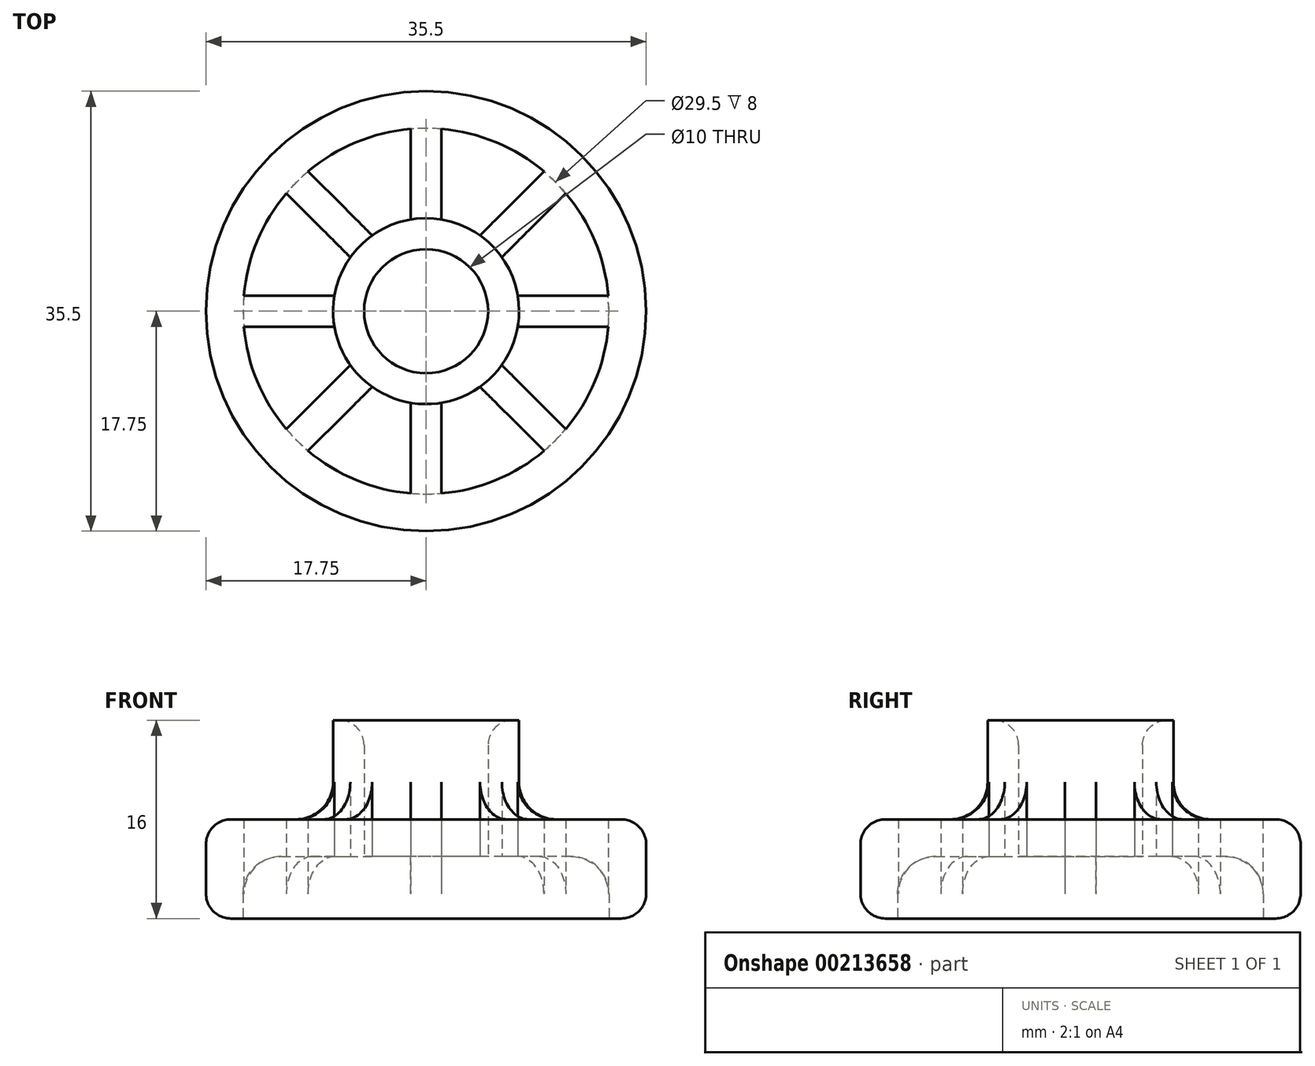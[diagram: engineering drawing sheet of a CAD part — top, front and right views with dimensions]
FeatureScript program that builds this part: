
annotation { "Feature Type Name" : "Feature", "Feature Type Description" : "" }
export const myFeature = defineFeature(function(context is Context, id is Id, definition is map)
    precondition{}
    {
        {
            var Q0;
            Q0=qCreatedBy(makeId("Top.planeOp"),FACE);
            var sketch = newSketch(context, id + "F0", { "sketchPlane" : qUnion([Q0])});
            skCircle(sketch, "E0", {"center": v(0, 0) * mm, "radius": 17.75 * mm});
            skCircle(sketch, "E1", {"center": v(0, 0) * mm, "radius": 14.75 * mm});
            skSolve(sketch);
        }
        {
            var Q0;
            Q0=makeQuery(id+"F0.imprint","IMPRINT",FACE,{"disambiguationData":[TD([[makeQuery(id+"F0.imprint","IMPRINT",EDGE,{"derivedFrom":sQuery(id+"F0.wireOp",EDGE,"E0")}),1.0]])]});
            extrude(context, id + "F1", {"entities" : qUnion([Q0]), "depth" : 8 * mm});
        }
        {
            var Q0;
            Q0=qCreatedBy(makeId("Top.planeOp"),FACE);
            cPlane(context, id + "F2", {"entities" : qUnion([Q0]), "cplaneType" : CPlaneType.OFFSET, "offset" : 5 * mm, "width" : 150 * mm, "height" : 150 * mm});
        }
        {
            var Q0;
            Q0=qCreatedBy(id+"F2.planeOp",FACE);
            var sketch = newSketch(context, id + "F3", { "sketchPlane" : qUnion([Q0])});
            skCircle(sketch, "E2", {"center": v(0, 0) * mm, "radius": 7.5 * mm});
            skCircle(sketch, "E3", {"center": v(0, 0) * mm, "radius": 5 * mm});
            skSolve(sketch);
        }
        {
            var Q0;
            Q0=makeQuery(id+"F3.imprint","IMPRINT",FACE,{"disambiguationData":[TD([[makeQuery(id+"F3.imprint","IMPRINT",EDGE,{"derivedFrom":sQuery(id+"F3.wireOp",EDGE,"E2")}),1.0]])]});
            extrude(context, id + "F4", {"entities" : qUnion([Q0]), "depth" : 11 * mm});
        }
        {
            var Q0;
            Q0=qCreatedBy(id+"F2.planeOp",FACE);
            var sketch = newSketch(context, id + "F5", { "sketchPlane" : qUnion([Q0])});
            skLineSegment(sketch, "E4.bottom", {"start": v(1.25, 15.28) * mm, "end": v(-1.25, 15.28) * mm});
            skLineSegment(sketch, "E4.top", {"start": v(1.25, 6.97) * mm, "end": v(-1.25, 6.97) * mm});
            skLineSegment(sketch, "E4.left", {"start": v(1.25, 15.28) * mm, "end": v(1.25, 6.97) * mm});
            skLineSegment(sketch, "E4.right", {"start": v(-1.25, 15.28) * mm, "end": v(-1.25, 6.97) * mm});
            skPoint(sketch, "E4.middle", {"position": v(0, 11.12) * mm});
            skSolve(sketch);
        }
        {
            var Q0;
            Q0=makeQuery(id+"F5.imprint","IMPRINT",FACE,{"disambiguationData":[TD([[makeQuery(id+"F5.imprint","IMPRINT",EDGE,{"derivedFrom":sQuery(id+"F5.wireOp",EDGE,"E4.bottom")}),1.0]])]});
            extrude(context, id + "F6", {"entities" : qUnion([Q0]), "depth" : 3 * mm});
        }
        {
            var Q0;
            Q0=qCreatedBy(makeId("Front.planeOp"),FACE);
            var sketch = newSketch(context, id + "F7", { "sketchPlane" : qUnion([Q0])});
            skLineSegment(sketch, "E5", {"start": v(0, 47.66) * mm, "end": v(0, -31.66) * mm, "construction": true});
            skSolve(sketch);
        }
        {
            var Q0;
            Q0=makeQuery(id+"F6.opExtrude","SWEPT_BODY",BODY,{"disambiguationData":[OSD([sQuery(id+"F5.wireOp",EDGE,"E4.bottom"),sQuery(id+"F5.wireOp",EDGE,"E4.top"),sQuery(id+"F5.wireOp",EDGE,"E4.left"),sQuery(id+"F5.wireOp",EDGE,"E4.right")])]});
            var Q1;
            Q1=sQuery(id+"F7.wireOp",EDGE,"E5");
            var Q2;
            Q2=makeQuery(id+"F6.opExtrude","SWEPT_BODY",BODY,{"disambiguationData":[OSD([sQuery(id+"F5.wireOp",EDGE,"E4.bottom"),sQuery(id+"F5.wireOp",EDGE,"E4.top"),sQuery(id+"F5.wireOp",EDGE,"E4.left"),sQuery(id+"F5.wireOp",EDGE,"E4.right")])]});
            circularPattern(context, id + "F8", {"operationType" : NewBodyOperationType.ADD, "entities" : qUnion([Q0]), "axis" : qUnion([Q1]), "angle" : 360 * degree, "instanceCount" : 8, "equalSpace" : true});
        }
        {
            var Q0;
            Q0=makeQuery(id+"F8.boolean.opBoolean","INTERSECT",EDGE,{"derivedFrom":[makeQuery(id+"F4.opExtrude","SWEPT_FACE",FACE,{"disambiguationData":[OSD([sQuery(id+"F3.wireOp",EDGE,"E2")])]}),makeQuery(id+"F8.opPattern","COPY",FACE,{"derivedFrom":makeQuery(id+"F6.opExtrude","CAP_FACE",FACE,{"disambiguationData":[OSD([sQuery(id+"F5.wireOp",EDGE,"E4.bottom"),sQuery(id+"F5.wireOp",EDGE,"E4.top"),sQuery(id+"F5.wireOp",EDGE,"E4.left"),sQuery(id+"F5.wireOp",EDGE,"E4.right")])],"isStart":false}),"instanceName":"1"})]});
            var Q1;
            Q1=makeQuery(id+"F8.boolean.opBoolean","INTERSECT",EDGE,{"derivedFrom":[makeQuery(id+"F4.opExtrude","SWEPT_FACE",FACE,{"disambiguationData":[OSD([sQuery(id+"F3.wireOp",EDGE,"E2")])]}),makeQuery(id+"F8.opPattern","COPY",FACE,{"derivedFrom":makeQuery(id+"F6.opExtrude","CAP_FACE",FACE,{"disambiguationData":[OSD([sQuery(id+"F5.wireOp",EDGE,"E4.bottom"),sQuery(id+"F5.wireOp",EDGE,"E4.top"),sQuery(id+"F5.wireOp",EDGE,"E4.left"),sQuery(id+"F5.wireOp",EDGE,"E4.right")])],"isStart":false}),"instanceName":"2"})]});
            var Q2;
            Q2=makeQuery(id+"F8.boolean.opBoolean","INTERSECT",EDGE,{"derivedFrom":[makeQuery(id+"F4.opExtrude","SWEPT_FACE",FACE,{"disambiguationData":[OSD([sQuery(id+"F3.wireOp",EDGE,"E2")])]}),makeQuery(id+"F8.opPattern","COPY",FACE,{"derivedFrom":makeQuery(id+"F6.opExtrude","CAP_FACE",FACE,{"disambiguationData":[OSD([sQuery(id+"F5.wireOp",EDGE,"E4.bottom"),sQuery(id+"F5.wireOp",EDGE,"E4.top"),sQuery(id+"F5.wireOp",EDGE,"E4.left"),sQuery(id+"F5.wireOp",EDGE,"E4.right")])],"isStart":false}),"instanceName":"3"})]});
            var Q3;
            Q3=makeQuery(id+"F8.boolean.opBoolean","INTERSECT",EDGE,{"derivedFrom":[makeQuery(id+"F4.opExtrude","SWEPT_FACE",FACE,{"disambiguationData":[OSD([sQuery(id+"F3.wireOp",EDGE,"E2")])]}),makeQuery(id+"F6.opExtrude","CAP_FACE",FACE,{"disambiguationData":[OSD([sQuery(id+"F5.wireOp",EDGE,"E4.bottom"),sQuery(id+"F5.wireOp",EDGE,"E4.top"),sQuery(id+"F5.wireOp",EDGE,"E4.left"),sQuery(id+"F5.wireOp",EDGE,"E4.right")])],"isStart":false})]});
            var Q4;
            Q4=makeQuery(id+"F8.boolean.opBoolean","INTERSECT",EDGE,{"derivedFrom":[makeQuery(id+"F4.opExtrude","SWEPT_FACE",FACE,{"disambiguationData":[OSD([sQuery(id+"F3.wireOp",EDGE,"E2")])]}),makeQuery(id+"F8.opPattern","COPY",FACE,{"derivedFrom":makeQuery(id+"F6.opExtrude","CAP_FACE",FACE,{"disambiguationData":[OSD([sQuery(id+"F5.wireOp",EDGE,"E4.bottom"),sQuery(id+"F5.wireOp",EDGE,"E4.top"),sQuery(id+"F5.wireOp",EDGE,"E4.left"),sQuery(id+"F5.wireOp",EDGE,"E4.right")])],"isStart":false}),"instanceName":"7"})]});
            var Q5;
            Q5=makeQuery(id+"F8.boolean.opBoolean","INTERSECT",EDGE,{"derivedFrom":[makeQuery(id+"F4.opExtrude","SWEPT_FACE",FACE,{"disambiguationData":[OSD([sQuery(id+"F3.wireOp",EDGE,"E2")])]}),makeQuery(id+"F8.opPattern","COPY",FACE,{"derivedFrom":makeQuery(id+"F6.opExtrude","CAP_FACE",FACE,{"disambiguationData":[OSD([sQuery(id+"F5.wireOp",EDGE,"E4.bottom"),sQuery(id+"F5.wireOp",EDGE,"E4.top"),sQuery(id+"F5.wireOp",EDGE,"E4.left"),sQuery(id+"F5.wireOp",EDGE,"E4.right")])],"isStart":false}),"instanceName":"6"})]});
            var Q6;
            Q6=makeQuery(id+"F8.boolean.opBoolean","INTERSECT",EDGE,{"derivedFrom":[makeQuery(id+"F4.opExtrude","SWEPT_FACE",FACE,{"disambiguationData":[OSD([sQuery(id+"F3.wireOp",EDGE,"E2")])]}),makeQuery(id+"F8.opPattern","COPY",FACE,{"derivedFrom":makeQuery(id+"F6.opExtrude","CAP_FACE",FACE,{"disambiguationData":[OSD([sQuery(id+"F5.wireOp",EDGE,"E4.bottom"),sQuery(id+"F5.wireOp",EDGE,"E4.top"),sQuery(id+"F5.wireOp",EDGE,"E4.left"),sQuery(id+"F5.wireOp",EDGE,"E4.right")])],"isStart":false}),"instanceName":"5"})]});
            var Q7;
            Q7=makeQuery(id+"F8.boolean.opBoolean","INTERSECT",EDGE,{"derivedFrom":[makeQuery(id+"F4.opExtrude","SWEPT_FACE",FACE,{"disambiguationData":[OSD([sQuery(id+"F3.wireOp",EDGE,"E2")])]}),makeQuery(id+"F8.opPattern","COPY",FACE,{"derivedFrom":makeQuery(id+"F6.opExtrude","CAP_FACE",FACE,{"disambiguationData":[OSD([sQuery(id+"F5.wireOp",EDGE,"E4.bottom"),sQuery(id+"F5.wireOp",EDGE,"E4.top"),sQuery(id+"F5.wireOp",EDGE,"E4.left"),sQuery(id+"F5.wireOp",EDGE,"E4.right")])],"isStart":false}),"instanceName":"4"})]});
            var Q8;
            Q8=makeQuery(id+"F8.boolean.opBoolean","INTERSECT",EDGE,{"disambiguationData":[OD(7.0)],"derivedFrom":[makeQuery(id+"F1.opExtrude","SWEPT_FACE",FACE,{"disambiguationData":[OSD([sQuery(id+"F0.wireOp",EDGE,"E1")])]}),makeQuery(id+"F8.opPattern","COPY",FACE,{"derivedFrom":makeQuery(id+"F6.opExtrude","CAP_FACE",FACE,{"disambiguationData":[OSD([sQuery(id+"F5.wireOp",EDGE,"E4.bottom"),sQuery(id+"F5.wireOp",EDGE,"E4.top"),sQuery(id+"F5.wireOp",EDGE,"E4.left"),sQuery(id+"F5.wireOp",EDGE,"E4.right")])],"isStart":true}),"instanceName":"7"})]});
            var Q9;
            Q9=makeQuery(id+"F8.boolean.opBoolean","INTERSECT",EDGE,{"disambiguationData":[OD(0.0)],"derivedFrom":[makeQuery(id+"F1.opExtrude","SWEPT_FACE",FACE,{"disambiguationData":[OSD([sQuery(id+"F0.wireOp",EDGE,"E1")])]}),makeQuery(id+"F8.opPattern","COPY",FACE,{"derivedFrom":makeQuery(id+"F6.opExtrude","CAP_FACE",FACE,{"disambiguationData":[OSD([sQuery(id+"F5.wireOp",EDGE,"E4.bottom"),sQuery(id+"F5.wireOp",EDGE,"E4.top"),sQuery(id+"F5.wireOp",EDGE,"E4.left"),sQuery(id+"F5.wireOp",EDGE,"E4.right")])],"isStart":true}),"instanceName":"7"})]});
            var Q10;
            Q10=makeQuery(id+"F8.boolean.opBoolean","INTERSECT",EDGE,{"disambiguationData":[OD(6.0)],"derivedFrom":[makeQuery(id+"F1.opExtrude","SWEPT_FACE",FACE,{"disambiguationData":[OSD([sQuery(id+"F0.wireOp",EDGE,"E1")])]}),makeQuery(id+"F8.opPattern","COPY",FACE,{"derivedFrom":makeQuery(id+"F6.opExtrude","CAP_FACE",FACE,{"disambiguationData":[OSD([sQuery(id+"F5.wireOp",EDGE,"E4.bottom"),sQuery(id+"F5.wireOp",EDGE,"E4.top"),sQuery(id+"F5.wireOp",EDGE,"E4.left"),sQuery(id+"F5.wireOp",EDGE,"E4.right")])],"isStart":true}),"instanceName":"7"})]});
            var Q11;
            Q11=makeQuery(id+"F8.boolean.opBoolean","INTERSECT",EDGE,{"disambiguationData":[OD(5.0)],"derivedFrom":[makeQuery(id+"F1.opExtrude","SWEPT_FACE",FACE,{"disambiguationData":[OSD([sQuery(id+"F0.wireOp",EDGE,"E1")])]}),makeQuery(id+"F8.opPattern","COPY",FACE,{"derivedFrom":makeQuery(id+"F6.opExtrude","CAP_FACE",FACE,{"disambiguationData":[OSD([sQuery(id+"F5.wireOp",EDGE,"E4.bottom"),sQuery(id+"F5.wireOp",EDGE,"E4.top"),sQuery(id+"F5.wireOp",EDGE,"E4.left"),sQuery(id+"F5.wireOp",EDGE,"E4.right")])],"isStart":true}),"instanceName":"7"})]});
            var Q12;
            Q12=makeQuery(id+"F8.boolean.opBoolean","INTERSECT",EDGE,{"disambiguationData":[OD(4.0)],"derivedFrom":[makeQuery(id+"F1.opExtrude","SWEPT_FACE",FACE,{"disambiguationData":[OSD([sQuery(id+"F0.wireOp",EDGE,"E1")])]}),makeQuery(id+"F8.opPattern","COPY",FACE,{"derivedFrom":makeQuery(id+"F6.opExtrude","CAP_FACE",FACE,{"disambiguationData":[OSD([sQuery(id+"F5.wireOp",EDGE,"E4.bottom"),sQuery(id+"F5.wireOp",EDGE,"E4.top"),sQuery(id+"F5.wireOp",EDGE,"E4.left"),sQuery(id+"F5.wireOp",EDGE,"E4.right")])],"isStart":true}),"instanceName":"7"})]});
            var Q13;
            Q13=makeQuery(id+"F8.boolean.opBoolean","INTERSECT",EDGE,{"disambiguationData":[OD(1.0)],"derivedFrom":[makeQuery(id+"F1.opExtrude","SWEPT_FACE",FACE,{"disambiguationData":[OSD([sQuery(id+"F0.wireOp",EDGE,"E1")])]}),makeQuery(id+"F8.opPattern","COPY",FACE,{"derivedFrom":makeQuery(id+"F6.opExtrude","CAP_FACE",FACE,{"disambiguationData":[OSD([sQuery(id+"F5.wireOp",EDGE,"E4.bottom"),sQuery(id+"F5.wireOp",EDGE,"E4.top"),sQuery(id+"F5.wireOp",EDGE,"E4.left"),sQuery(id+"F5.wireOp",EDGE,"E4.right")])],"isStart":true}),"instanceName":"7"})]});
            var Q14;
            Q14=makeQuery(id+"F8.boolean.opBoolean","INTERSECT",EDGE,{"disambiguationData":[OD(2.0)],"derivedFrom":[makeQuery(id+"F1.opExtrude","SWEPT_FACE",FACE,{"disambiguationData":[OSD([sQuery(id+"F0.wireOp",EDGE,"E1")])]}),makeQuery(id+"F8.opPattern","COPY",FACE,{"derivedFrom":makeQuery(id+"F6.opExtrude","CAP_FACE",FACE,{"disambiguationData":[OSD([sQuery(id+"F5.wireOp",EDGE,"E4.bottom"),sQuery(id+"F5.wireOp",EDGE,"E4.top"),sQuery(id+"F5.wireOp",EDGE,"E4.left"),sQuery(id+"F5.wireOp",EDGE,"E4.right")])],"isStart":true}),"instanceName":"7"})]});
            var Q15;
            Q15=makeQuery(id+"F8.boolean.opBoolean","INTERSECT",EDGE,{"disambiguationData":[OD(3.0)],"derivedFrom":[makeQuery(id+"F1.opExtrude","SWEPT_FACE",FACE,{"disambiguationData":[OSD([sQuery(id+"F0.wireOp",EDGE,"E1")])]}),makeQuery(id+"F8.opPattern","COPY",FACE,{"derivedFrom":makeQuery(id+"F6.opExtrude","CAP_FACE",FACE,{"disambiguationData":[OSD([sQuery(id+"F5.wireOp",EDGE,"E4.bottom"),sQuery(id+"F5.wireOp",EDGE,"E4.top"),sQuery(id+"F5.wireOp",EDGE,"E4.left"),sQuery(id+"F5.wireOp",EDGE,"E4.right")])],"isStart":true}),"instanceName":"7"})]});
            fillet(context, id + "F9", {"entities" : qUnion([Q0, Q1, Q2, Q3, Q4, Q5, Q6, Q7, Q8, Q9, Q10, Q11, Q12, Q13, Q14, Q15]), "radius" : 3 * mm, "tangentPropagation" : true, "allowEdgeOverflow" : false});
        }
        {
            var Q0;
            Q0=makeQuery(id+"F1.opExtrude","CAP_EDGE",EDGE,{"disambiguationData":[OSD([sQuery(id+"F0.wireOp",EDGE,"E0")])],"isStart":false});
            var Q1;
            Q1=makeQuery(id+"F1.opExtrude","CAP_EDGE",EDGE,{"disambiguationData":[OSD([sQuery(id+"F0.wireOp",EDGE,"E0")])],"isStart":true});
            var Q2;
            Q2=makeQuery(id+"F4.opExtrude","CAP_EDGE",EDGE,{"disambiguationData":[OSD([sQuery(id+"F3.wireOp",EDGE,"E3")])],"isStart":false});
            fillet(context, id + "F10", {"entities" : qUnion([Q0, Q1, Q2]), "radius" : 2 * mm, "tangentPropagation" : true, "allowEdgeOverflow" : false});
        }
    });
